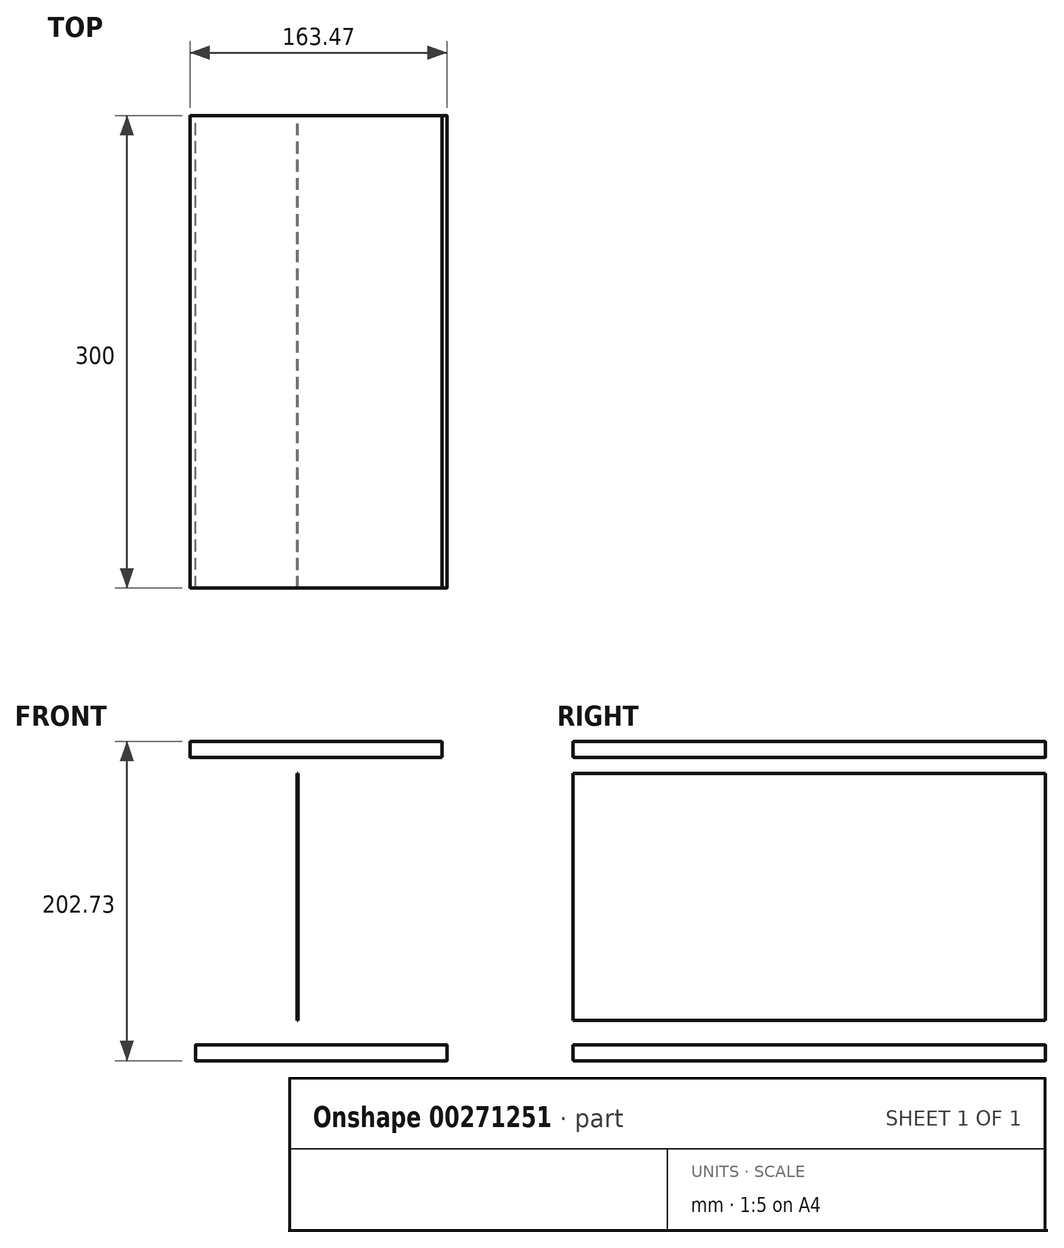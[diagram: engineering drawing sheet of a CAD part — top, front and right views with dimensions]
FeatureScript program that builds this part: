
annotation { "Feature Type Name" : "Feature", "Feature Type Description" : "" }
export const myFeature = defineFeature(function(context is Context, id is Id, definition is map)
    precondition{}
    {
        {
            var Q0;
            Q0=qCreatedBy(makeId("Front.planeOp"),FACE);
            var sketch = newSketch(context, id + "F0", { "sketchPlane" : qUnion([Q0])});
            skLineSegment(sketch, "E0.bottom", {"start": v(-76.75, -76.96) * mm, "end": v(83.25, -76.96) * mm});
            skLineSegment(sketch, "E0.top", {"start": v(-76.75, -86.96) * mm, "end": v(83.25, -86.96) * mm});
            skLineSegment(sketch, "E0.left", {"start": v(-76.75, -76.96) * mm, "end": v(-76.75, -86.96) * mm});
            skLineSegment(sketch, "E0.right", {"start": v(83.25, -76.96) * mm, "end": v(83.25, -86.96) * mm});
            skLineSegment(sketch, "E1.bottom", {"start": v(-12.12, 95.52) * mm, "end": v(-11.55, 95.52) * mm});
            skLineSegment(sketch, "E1.top", {"start": v(-12.12, -61.48) * mm, "end": v(-11.55, -61.48) * mm});
            skLineSegment(sketch, "E1.left", {"start": v(-12.12, 95.52) * mm, "end": v(-12.12, -61.48) * mm});
            skLineSegment(sketch, "E1.right", {"start": v(-11.55, 95.52) * mm, "end": v(-11.55, -61.48) * mm});
            skLineSegment(sketch, "E2.bottom", {"start": v(-80.22, 115.77) * mm, "end": v(79.78, 115.77) * mm});
            skLineSegment(sketch, "E2.top", {"start": v(-80.22, 105.77) * mm, "end": v(79.78, 105.77) * mm});
            skLineSegment(sketch, "E2.left", {"start": v(-80.22, 115.77) * mm, "end": v(-80.22, 105.77) * mm});
            skLineSegment(sketch, "E2.right", {"start": v(79.78, 115.77) * mm, "end": v(79.78, 105.77) * mm});
            skSolve(sketch);
        }
        {
            var Q0;
            Q0 = qSketchRegion(id + "F0", true);
            extrude(context, id + "F1", {"entities" : qUnion([Q0]), "depth" : 300 * mm});
        }
        {
            var Q0;
            Q0=makeQuery(id+"F1.opExtrude","SWEPT_EDGE",EDGE,{"disambiguationData":[OSD([sQuery(id+"F0.wireOp",EDGE,"E2.bottom"),sQuery(id+"F0.wireOp",EDGE,"E2.left")])]});
            var Q1;
            Q1=makeQuery(id+"F1.opExtrude","SWEPT_EDGE",EDGE,{"disambiguationData":[OSD([sQuery(id+"F0.wireOp",EDGE,"E2.bottom"),sQuery(id+"F0.wireOp",EDGE,"E2.right")])]});
            var Q2;
            Q2=makeQuery(id+"F1.opExtrude","SWEPT_EDGE",EDGE,{"disambiguationData":[OSD([sQuery(id+"F0.wireOp",EDGE,"E2.top"),sQuery(id+"F0.wireOp",EDGE,"E2.right")])]});
            var Q3;
            Q3=makeQuery(id+"F1.opExtrude","CAP_EDGE",EDGE,{"disambiguationData":[OSD([sQuery(id+"F0.wireOp",EDGE,"E2.bottom")])],"isStart":true});
            var Q4;
            Q4=makeQuery(id+"F1.opExtrude","CAP_EDGE",EDGE,{"disambiguationData":[OSD([sQuery(id+"F0.wireOp",EDGE,"E2.top")])],"isStart":true});
            var Q5;
            Q5=makeQuery(id+"F1.opExtrude","SWEPT_EDGE",EDGE,{"disambiguationData":[OSD([sQuery(id+"F0.wireOp",EDGE,"E2.top"),sQuery(id+"F0.wireOp",EDGE,"E2.left")])]});
            var Q6;
            Q6=makeQuery(id+"F1.opExtrude","CAP_EDGE",EDGE,{"disambiguationData":[OSD([sQuery(id+"F0.wireOp",EDGE,"E2.bottom")])],"isStart":false});
            var Q7;
            Q7=makeQuery(id+"F1.opExtrude","CAP_EDGE",EDGE,{"disambiguationData":[OSD([sQuery(id+"F0.wireOp",EDGE,"E2.top")])],"isStart":false});
            var Q8;
            Q8=makeQuery(id+"F1.opExtrude","CAP_EDGE",EDGE,{"disambiguationData":[OSD([sQuery(id+"F0.wireOp",EDGE,"E2.left")])],"isStart":false});
            var Q9;
            Q9=makeQuery(id+"F1.opExtrude","CAP_EDGE",EDGE,{"disambiguationData":[OSD([sQuery(id+"F0.wireOp",EDGE,"E2.right")])],"isStart":false});
            var Q10;
            Q10=makeQuery(id+"F1.opExtrude","SWEPT_FACE",FACE,{"disambiguationData":[OSD([sQuery(id+"F0.wireOp",EDGE,"E2.top")])]});
            var Q11;
            Q11=makeQuery(id+"F1.opExtrude","CAP_EDGE",EDGE,{"disambiguationData":[OSD([sQuery(id+"F0.wireOp",EDGE,"E2.right")])],"isStart":true});
            var Q12;
            Q12=makeQuery(id+"F1.opExtrude","CAP_EDGE",EDGE,{"disambiguationData":[OSD([sQuery(id+"F0.wireOp",EDGE,"E2.left")])],"isStart":true});
            var Q13;
            Q13=makeQuery(id+"F1.opExtrude","CAP_EDGE",EDGE,{"disambiguationData":[OSD([sQuery(id+"F0.wireOp",EDGE,"E0.top")])],"isStart":false});
            var Q14;
            Q14=makeQuery(id+"F1.opExtrude","CAP_EDGE",EDGE,{"disambiguationData":[OSD([sQuery(id+"F0.wireOp",EDGE,"E0.bottom")])],"isStart":false});
            var Q15;
            Q15=makeQuery(id+"F1.opExtrude","CAP_EDGE",EDGE,{"disambiguationData":[OSD([sQuery(id+"F0.wireOp",EDGE,"E0.left")])],"isStart":false});
            var Q16;
            Q16=makeQuery(id+"F1.opExtrude","CAP_EDGE",EDGE,{"disambiguationData":[OSD([sQuery(id+"F0.wireOp",EDGE,"E0.right")])],"isStart":false});
            var Q17;
            Q17=makeQuery(id+"F1.opExtrude","SWEPT_FACE",FACE,{"disambiguationData":[OSD([sQuery(id+"F0.wireOp",EDGE,"E0.right")])]});
            var Q18;
            Q18=makeQuery(id+"F1.opExtrude","SWEPT_EDGE",EDGE,{"disambiguationData":[OSD([sQuery(id+"F0.wireOp",EDGE,"E0.top"),sQuery(id+"F0.wireOp",EDGE,"E0.right")])]});
            var Q19;
            Q19=makeQuery(id+"F1.opExtrude","SWEPT_EDGE",EDGE,{"disambiguationData":[OSD([sQuery(id+"F0.wireOp",EDGE,"E0.bottom"),sQuery(id+"F0.wireOp",EDGE,"E0.right")])]});
            var Q20;
            Q20=makeQuery(id+"F1.opExtrude","CAP_EDGE",EDGE,{"disambiguationData":[OSD([sQuery(id+"F0.wireOp",EDGE,"E0.right")])],"isStart":true});
            var Q21;
            Q21=makeQuery(id+"F1.opExtrude","CAP_EDGE",EDGE,{"disambiguationData":[OSD([sQuery(id+"F0.wireOp",EDGE,"E0.top")])],"isStart":true});
            var Q22;
            Q22=makeQuery(id+"F1.opExtrude","CAP_EDGE",EDGE,{"disambiguationData":[OSD([sQuery(id+"F0.wireOp",EDGE,"E0.bottom")])],"isStart":true});
            var Q23;
            Q23=makeQuery(id+"F1.opExtrude","CAP_EDGE",EDGE,{"disambiguationData":[OSD([sQuery(id+"F0.wireOp",EDGE,"E0.left")])],"isStart":true});
            var Q24;
            Q24=makeQuery(id+"F1.opExtrude","SWEPT_EDGE",EDGE,{"disambiguationData":[OSD([sQuery(id+"F0.wireOp",EDGE,"E0.bottom"),sQuery(id+"F0.wireOp",EDGE,"E0.left")])]});
            var Q25;
            Q25=makeQuery(id+"F1.opExtrude","SWEPT_EDGE",EDGE,{"disambiguationData":[OSD([sQuery(id+"F0.wireOp",EDGE,"E0.top"),sQuery(id+"F0.wireOp",EDGE,"E0.left")])]});
            fillet(context, id + "F2", {"entities" : qUnion([Q0, Q1, Q2, Q3, Q4, Q5, Q6, Q7, Q8, Q9, Q10, Q11, Q12, Q13, Q14, Q15, Q16, Q17, Q18, Q19, Q20, Q21, Q22, Q23, Q24, Q25]), "radius" : 0.2 * mm, "tangentPropagation" : true, "allowEdgeOverflow" : false});
        }
    });
